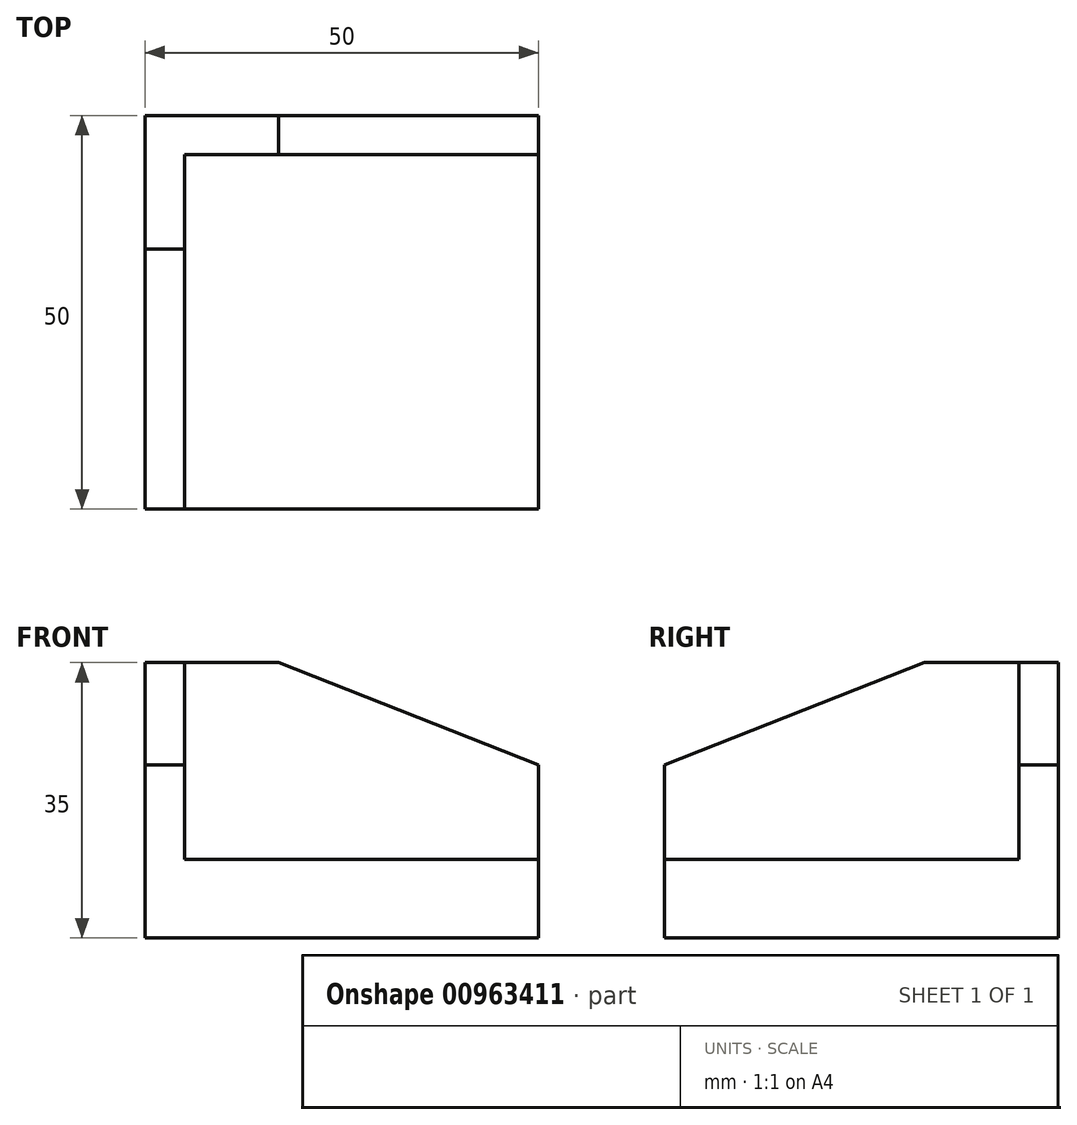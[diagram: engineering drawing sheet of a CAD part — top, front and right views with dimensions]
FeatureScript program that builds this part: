
annotation { "Feature Type Name" : "Feature", "Feature Type Description" : "" }
export const myFeature = defineFeature(function(context is Context, id is Id, definition is map)
    precondition{}
    {
        {
            var Q0;
            Q0=qCreatedBy(makeId("Top.planeOp"),FACE);
            var sketch = newSketch(context, id + "F0", { "sketchPlane" : qUnion([Q0])});
            skLineSegment(sketch, "E0.bottom", {"start": v(25, -25) * mm, "end": v(-25, -25) * mm});
            skLineSegment(sketch, "E0.top", {"start": v(25, 25) * mm, "end": v(-25, 25) * mm});
            skLineSegment(sketch, "E0.left", {"start": v(25, -25) * mm, "end": v(25, 25) * mm});
            skLineSegment(sketch, "E0.right", {"start": v(-25, -25) * mm, "end": v(-25, 25) * mm});
            skPoint(sketch, "E0.middle", {"position": v(0, 0) * mm});
            skSolve(sketch);
        }
        {
            var Q0;
            Q0=makeQuery(id+"F0.imprint","IMPRINT",FACE,{"disambiguationData":[TD([[makeQuery(id+"F0.imprint","IMPRINT",EDGE,{"derivedFrom":sQuery(id+"F0.wireOp",EDGE,"E0.bottom")}),-1.0]])]});
            extrude(context, id + "F1", {"entities" : qUnion([Q0]), "depth" : 5 * mm, "offsetDistance" : 25 * mm});
        }
        {
            var Q0;
            Q0=makeQuery(id+"F1.opExtrude","CAP_FACE",FACE,{"disambiguationData":[OSD([sQuery(id+"F0.wireOp",EDGE,"E0.bottom"),sQuery(id+"F0.wireOp",EDGE,"E0.top"),sQuery(id+"F0.wireOp",EDGE,"E0.left"),sQuery(id+"F0.wireOp",EDGE,"E0.right")])],"isStart":false});
            var sketch = newSketch(context, id + "F2", { "sketchPlane" : qUnion([Q0])});
            skLineSegment(sketch, "E1.bottom", {"start": v(-25, 25) * mm, "end": v(25, 25) * mm});
            skLineSegment(sketch, "E1.top", {"start": v(-25, 20) * mm, "end": v(25, 20) * mm});
            skLineSegment(sketch, "E1.left", {"start": v(-25, 25) * mm, "end": v(-25, 20) * mm});
            skLineSegment(sketch, "E1.right", {"start": v(25, 25) * mm, "end": v(25, 20) * mm});
            skSolve(sketch);
        }
        {
            var Q0;
            Q0 = qSketchRegion(id + "F2", true);
            extrude(context, id + "F3", {"entities" : qUnion([Q0]), "operationType" : NewBodyOperationType.ADD, "depth" : 25 * mm, "offsetDistance" : 25 * mm});
        }
        {
            var Q0;
            Q0=makeQuery(id+"F1.opExtrude","CAP_FACE",FACE,{"disambiguationData":[OSD([sQuery(id+"F0.wireOp",EDGE,"E0.bottom"),sQuery(id+"F0.wireOp",EDGE,"E0.top"),sQuery(id+"F0.wireOp",EDGE,"E0.left"),sQuery(id+"F0.wireOp",EDGE,"E0.right")])],"isStart":false});
            var sketch = newSketch(context, id + "F4", { "sketchPlane" : qUnion([Q0])});
            skLineSegment(sketch, "E2.bottom", {"start": v(-25, -25) * mm, "end": v(-20, -25) * mm});
            skLineSegment(sketch, "E2.top", {"start": v(-25, 25) * mm, "end": v(-20, 25) * mm});
            skLineSegment(sketch, "E2.left", {"start": v(-25, -25) * mm, "end": v(-25, 25) * mm});
            skLineSegment(sketch, "E2.right", {"start": v(-20, -25) * mm, "end": v(-20, 25) * mm});
            skSolve(sketch);
        }
        {
            var Q0;
            {var subQ0=sQuery(id+"F4.wireOp",EDGE,"E2.bottom");Q0=makeQuery(id+"F4.imprint","IMPRINT",FACE,{"disambiguationData":[TD([[makeQuery(id+"F4.imprint","IMPRINT",EDGE,{"derivedFrom":subQ0}),-1.0]])]});}
            extrude(context, id + "F5", {"entities" : qUnion([Q0]), "operationType" : NewBodyOperationType.ADD, "depth" : 25 * mm, "offsetDistance" : 25 * mm});
        }
        {
            var Q0;
            Q0=makeQuery(id+"F3.boolean.opBoolean","MERGE",FACE,{"derivedFrom":[makeQuery(id+"F1.opExtrude","SWEPT_FACE",FACE,{"disambiguationData":[OSD([sQuery(id+"F0.wireOp",EDGE,"E0.top")])]}),makeQuery(id+"F3.opExtrude","SWEPT_FACE",FACE,{"disambiguationData":[OSD([sQuery(id+"F2.wireOp",EDGE,"E1.bottom")])]})]});
            var sketch = newSketch(context, id + "F6", { "sketchPlane" : qUnion([Q0])});
            skLineSegment(sketch, "E3", {"start": v(-25, 30) * mm, "end": v(25, 30) * mm, "construction": true});
            skLineSegment(sketch, "E4", {"start": v(25, 30) * mm, "end": v(25, 0) * mm, "construction": true});
            skLineSegment(sketch, "E5", {"start": v(25, 0) * mm, "end": v(-25, 0) * mm, "construction": true});
            skLineSegment(sketch, "E6", {"start": v(-25, 0) * mm, "end": v(-25, 30) * mm, "construction": true});
            skPoint(sketch, "E7", {"position": v(8, 30) * mm});
            skPoint(sketch, "E8", {"position": v(-25, 17) * mm});
            skLineSegment(sketch, "E9", {"start": v(-25, 17) * mm, "end": v(8, 30) * mm});
            skLineSegment(sketch, "E10", {"start": v(8, 30) * mm, "end": v(-25, 30) * mm});
            skLineSegment(sketch, "E11", {"start": v(-25, 30) * mm, "end": v(-25, 17) * mm});
            skSolve(sketch);
        }
        {
            var Q0;
            Q0=makeQuery(id+"F6.imprint","IMPRINT",FACE,{"disambiguationData":[TD([[makeQuery(id+"F6.imprint","IMPRINT",EDGE,{"derivedFrom":sQuery(id+"F6.wireOp",EDGE,"E9")}),1.0]])]});
            extrude(context, id + "F7", {"entities" : qUnion([Q0]), "operationType" : NewBodyOperationType.REMOVE, "oppositeDirection" : true, "depth" : 5 * mm, "offsetDistance" : 25 * mm});
        }
        {
            var Q0;
            Q0=makeQuery(id+"F5.boolean.opBoolean","MERGE",FACE,{"derivedFrom":[makeQuery(id+"F3.boolean.opBoolean","MERGE",FACE,{"derivedFrom":[makeQuery(id+"F1.opExtrude","SWEPT_FACE",FACE,{"disambiguationData":[OSD([sQuery(id+"F0.wireOp",EDGE,"E0.right")])]}),makeQuery(id+"F3.opExtrude","SWEPT_FACE",FACE,{"disambiguationData":[OSD([sQuery(id+"F2.wireOp",EDGE,"E1.left")])]})]}),makeQuery(id+"F5.opExtrude","SWEPT_FACE",FACE,{"disambiguationData":[OSD([sQuery(id+"F4.wireOp",EDGE,"E2.left")])]})]});
            var sketch = newSketch(context, id + "F8", { "sketchPlane" : qUnion([Q0])});
            skLineSegment(sketch, "E12", {"start": v(-25, 30) * mm, "end": v(25, 30) * mm, "construction": true});
            skLineSegment(sketch, "E13", {"start": v(25, 30) * mm, "end": v(25, 0) * mm, "construction": true});
            skLineSegment(sketch, "E14", {"start": v(25, 0) * mm, "end": v(-25, 0) * mm, "construction": true});
            skLineSegment(sketch, "E15", {"start": v(-25, 0) * mm, "end": v(-25, 30) * mm, "construction": true});
            skPoint(sketch, "E16", {"position": v(-8, 30) * mm});
            skPoint(sketch, "E17", {"position": v(25, 17) * mm});
            skLineSegment(sketch, "E18", {"start": v(-8, 30) * mm, "end": v(25, 17) * mm});
            skLineSegment(sketch, "E19", {"start": v(25, 17) * mm, "end": v(25, 30) * mm});
            skLineSegment(sketch, "E20", {"start": v(25, 30) * mm, "end": v(-8, 30) * mm});
            skSolve(sketch);
        }
        {
            var Q0;
            Q0=makeQuery(id+"F8.imprint","IMPRINT",FACE,{"disambiguationData":[TD([[makeQuery(id+"F8.imprint","IMPRINT",EDGE,{"derivedFrom":sQuery(id+"F8.wireOp",EDGE,"E18")}),1.0]])]});
            extrude(context, id + "F9", {"entities" : qUnion([Q0]), "operationType" : NewBodyOperationType.REMOVE, "oppositeDirection" : true, "depth" : 5 * mm, "offsetDistance" : 25 * mm});
        }
        {
            var Q0;
            Q0=makeQuery(id+"F1.opExtrude","CAP_FACE",FACE,{"disambiguationData":[OSD([sQuery(id+"F0.wireOp",EDGE,"E0.bottom"),sQuery(id+"F0.wireOp",EDGE,"E0.top"),sQuery(id+"F0.wireOp",EDGE,"E0.left"),sQuery(id+"F0.wireOp",EDGE,"E0.right")])],"isStart":true});
            var sketch = newSketch(context, id + "F10", { "sketchPlane" : qUnion([Q0])});
            skLineSegment(sketch, "E21.bottom", {"start": v(-25, 25) * mm, "end": v(25, 25) * mm});
            skLineSegment(sketch, "E21.top", {"start": v(-25, -25) * mm, "end": v(25, -25) * mm});
            skLineSegment(sketch, "E21.left", {"start": v(-25, 25) * mm, "end": v(-25, -25) * mm});
            skLineSegment(sketch, "E21.right", {"start": v(25, 25) * mm, "end": v(25, -25) * mm});
            skSolve(sketch);
        }
        {
            var Q0;
            Q0 = qSketchRegion(id + "F10", true);
            extrude(context, id + "F11", {"entities" : qUnion([Q0]), "operationType" : NewBodyOperationType.ADD, "depth" : 5 * mm, "offsetDistance" : 25 * mm});
        }
    });
